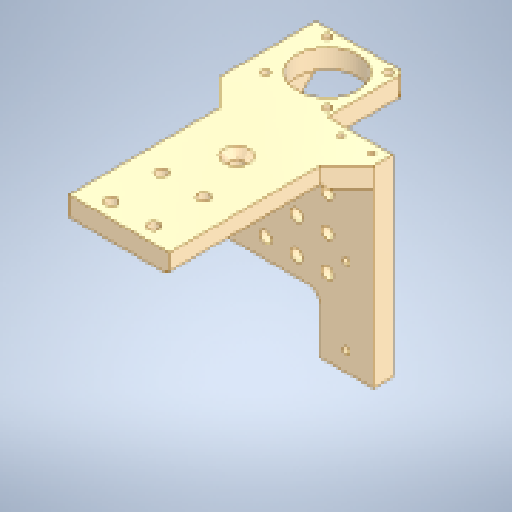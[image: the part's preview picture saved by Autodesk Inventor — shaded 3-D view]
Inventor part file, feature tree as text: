
AUTODESK INVENTOR PART (.ipt)
format: ipt  version: 2024.1 (Build 281209000, 209)  size: 448,512 bytes
history: native  units: in
note: dims shown in document units (in); Inventor stores cm internally (conversion verified against a paired STEP export)
features: extrude x12, sketch x12, fillet x5, chamfer x4
ambient origin geometry x8: Origin, YZ Plane, XZ Plane, XY Plane, X Axis, Y Axis, Z Axis, Center Point
bodies: Solid1 (feature_tree)
feature tree (33):
  extrude  "Extrusion1"  Depth=1.378in
  extrude  "Extrusion2"  Depth=0.1969in
  extrude  "Extrusion3"  Depth=0.7874in TaperAngle=0.0deg
  extrude  "Extrusion4"  Depth=0.7874in
  fillet  "Fillet1"  Radius=0.7874in
  extrude  "Extrusion5"  Depth=0.3937in
  fillet  "Fillet2"  Radius=0.3937in
  fillet  "Fillet4"  Radius=0.0787in
  extrude  "Extrusion6"  Depth=0.0787in
  chamfer  "Chamfer2"  Distance=0.315in
  extrude  "Extrusion7"  Depth=0.2756in
  chamfer  "Chamfer3"  Distance=0.315in
  extrude  "Extrusion8"  TaperAngle=0.0deg  [1 undecoded]
  chamfer  "Chamfer4"  Distance=0.0591in
  fillet  "Fillet5"  [1 undecoded]
  extrude  "Extrusion9"  Depth=0.1969in
  extrude  "Extrusion10"  Depth=0.0787in
  fillet  "Fillet6"  Radius=0.1969in
  extrude  "Extrusion11"  Depth=0.2756in
  chamfer  "Chamfer7"  Distance=0.2756in
  extrude  "Extrusion12"  Depth=1.811in TaperAngle=0.0deg
  sketch  "Sketch1"  dims[d0=1.5748in d1=1.378in]
  sketch  "Sketch2"  dims[d2=0.1969in d3=0.0in d4=0.9055in]
  sketch  "Sketch3"  dims[d5=0.1969in d6=0.7874in d7=0.0in]
  sketch  "Sketch4"  dims[d8=0.7874in d9=0.1181in d10=0.7874in d11=0.0in]
  sketch  "Sketch5"  dims[d12=0.6299in d13=0.3937in d14=0.3937in d15=0.0787in]
  sketch  "Sketch6"  dims[d16=0.0787in d17=0.0787in]
  sketch  "Sketch7"  dims[d18=0.0787in]
  sketch  "Sketch8"  dims[d19=0.315in]
  sketch  "Sketch9"  dims[d20=0.315in]
  sketch  "Sketch10"  dims[d21=0.315in]
  sketch  "Sketch11"  dims[d22=0.315in]
  sketch  "Sketch12"  dims[d23=0.315in d24=0.315in d25=0.315in d26=0.315in d27=0.0in d28=0.0in d29=0.0591in d30=0.0in d31=0.0in d32=0.1969in d34=0.0787in d39=0.1969in d40=0.2756in d41=0.2756in d42=1.811in d43=0.0in d44=0.2756in d45=0.0787in d46=45.0deg d47=0.1181in d48=0.6102in d49=0.5118in d50=0.0in d51=0.0in d52=0.0709in d53=0.0787in d54=45.0deg d55=0.063in d56=0.063in d57=0.0984in d58=0.0984in d59=0.1181in d60=0.315in d61=0.3937in d62=0.0in d63=0.0315in d64=0.0787in d65=45.0deg d66=0.0394in d67=0.5512in d68=0.5906in d69=0.0in d70=0.063in d71=0.2756in d72=0.1969in d73=1.1811in d75=0.7874in d76=0.3937in d78=0.3937in d80=0.0in d81=0.0in d88=0.1181in d89=0.1181in d90=0.1181in d91=0.1181in d92=0.1181in d93=0.1181in d94=0.1181in d95=0.1969in d96=0.1969in d97=0.315in d98=0.4724in d99=0.4724in d100=0.4724in d101=0.3543in d102=0.3543in d103=0.3543in d104=0.315in d105=0.3543in d106=0.315in d107=0.0in d108=0.0in d109=0.315in d110=0.1181in d111=0.1969in d112=0.3543in d113=0.3543in d114=0.1181in d115=0.1181in d116=0.315in d117=0.315in d118=0.0748in d119=0.0787in d120=45.0deg d121=0.1181in d122=0.1181in d123=0.1181in d124=0.1181in d125=0.6693in d126=0.6693in d127=0.315in d128=0.315in d129=0.2756in d130=0.2756in d131=0.1575in d132=0.1575in d133=0.0in d134=0.0in]
note: 2 required parameter values undecoded (feature->parameter linkage not recoverable at this tier; creation-order binding heuristic only, values carry confidence <= 0.55)
